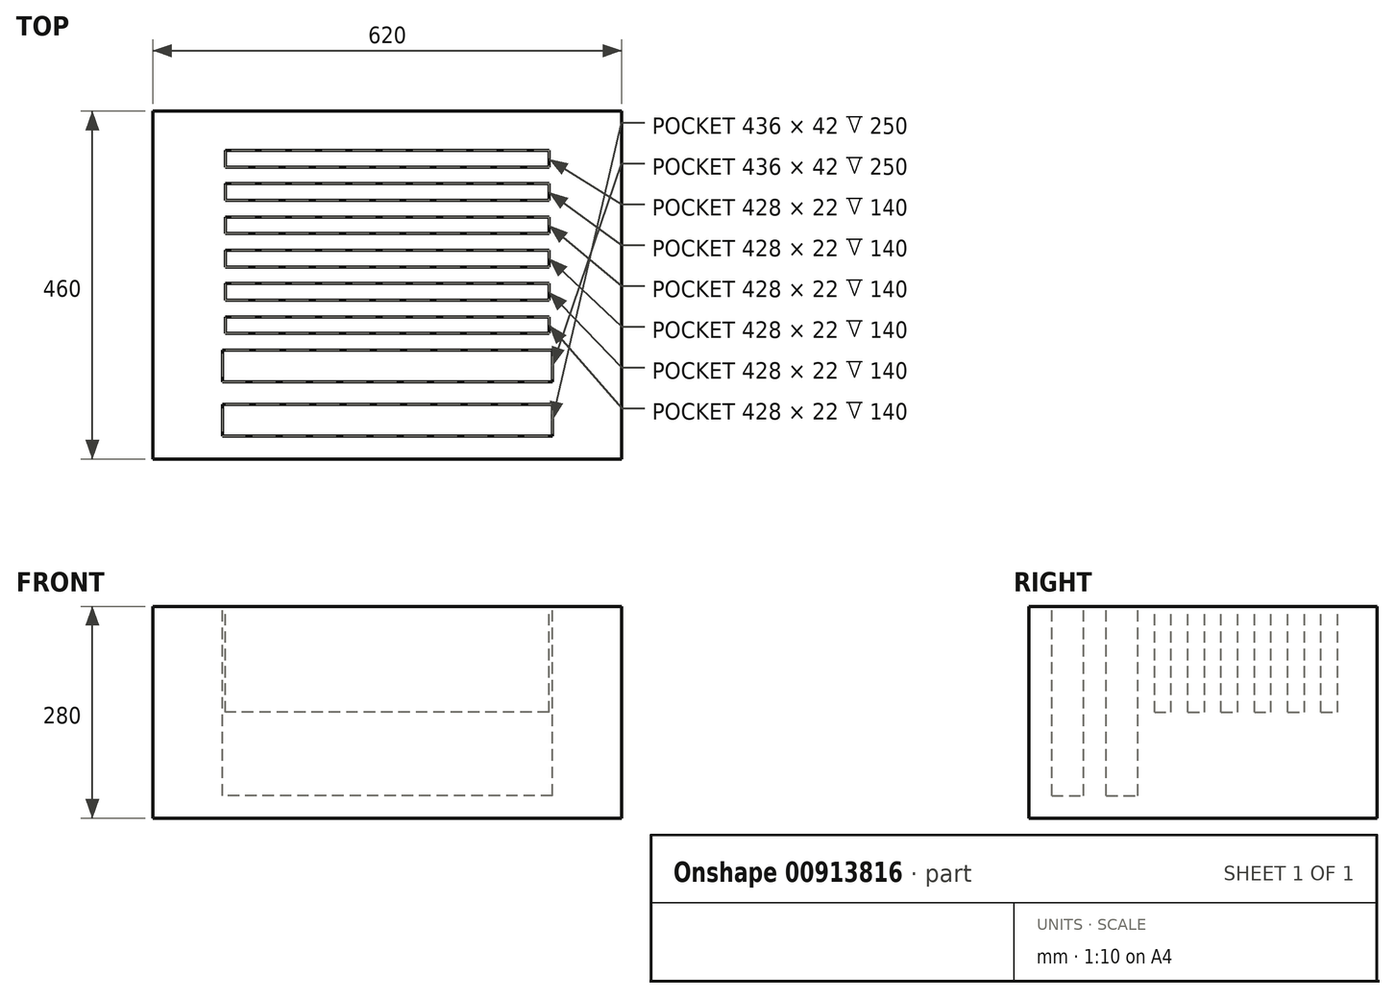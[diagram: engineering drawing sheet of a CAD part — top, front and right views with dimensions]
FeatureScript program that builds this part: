
annotation { "Feature Type Name" : "Feature", "Feature Type Description" : "" }
export const myFeature = defineFeature(function(context is Context, id is Id, definition is map)
    precondition{}
    {
        {
            var Q0;
            Q0=qCreatedBy(makeId("Top.planeOp"),FACE);
            var sketch = newSketch(context, id + "F0", { "sketchPlane" : qUnion([Q0])});
            skLineSegment(sketch, "E0.bottom", {"start": v(310.34, -166) * mm, "end": v(-309.66, -166) * mm});
            skLineSegment(sketch, "E0.top", {"start": v(310.34, 294) * mm, "end": v(-309.66, 294) * mm});
            skLineSegment(sketch, "E0.left", {"start": v(310.34, -166) * mm, "end": v(310.34, 294) * mm});
            skLineSegment(sketch, "E0.right", {"start": v(-309.66, -166) * mm, "end": v(-309.66, 294) * mm});
            skLineSegment(sketch, "E1.bottom", {"start": v(218.34, -136) * mm, "end": v(-217.66, -136) * mm});
            skLineSegment(sketch, "E1.top", {"start": v(218.34, -94) * mm, "end": v(-217.66, -94) * mm});
            skLineSegment(sketch, "E1.left", {"start": v(218.34, -136) * mm, "end": v(218.34, -94) * mm});
            skLineSegment(sketch, "E1.right", {"start": v(-217.66, -136) * mm, "end": v(-217.66, -94) * mm});
            skPoint(sketch, "E1.middle", {"position": v(0, 0) * mm});
            skLineSegment(sketch, "E2.0.1.0", {"start": v(218.34, -64) * mm, "end": v(218.34, -22) * mm});
            skLineSegment(sketch, "E2.0.1.1", {"start": v(218.34, -64) * mm, "end": v(-217.66, -64) * mm});
            skLineSegment(sketch, "E2.0.1.2", {"start": v(218.34, -22) * mm, "end": v(-217.66, -22) * mm});
            skLineSegment(sketch, "E2.0.1.3", {"start": v(-217.66, -64) * mm, "end": v(-217.66, -22) * mm});
            skLineSegment(sketch, "E2.direction1", {"start": v(-217.66, -136) * mm, "end": v(-182.5, -136) * mm, "construction": true});
            skLineSegment(sketch, "E2.direction2", {"start": v(-217.66, -136) * mm, "end": v(-217.66, -64) * mm, "construction": true});
            skLineSegment(sketch, "E3.bottom", {"start": v(214, 0) * mm, "end": v(-214, 0) * mm});
            skLineSegment(sketch, "E3.top", {"start": v(214, 22) * mm, "end": v(-214, 22) * mm});
            skLineSegment(sketch, "E3.left", {"start": v(214, 0) * mm, "end": v(214, 22) * mm});
            skLineSegment(sketch, "E3.right", {"start": v(-214, 0) * mm, "end": v(-214, 22) * mm});
            skPoint(sketch, "E3.middle", {"position": v(0, 11) * mm});
            skLineSegment(sketch, "E4.0.1.0", {"start": v(-214, 44) * mm, "end": v(-214, 66) * mm});
            skLineSegment(sketch, "E4.0.1.1", {"start": v(214, 44) * mm, "end": v(-214, 44) * mm});
            skLineSegment(sketch, "E4.0.1.2", {"start": v(214, 66) * mm, "end": v(-214, 66) * mm});
            skLineSegment(sketch, "E4.0.1.3", {"start": v(214, 44) * mm, "end": v(214, 66) * mm});
            skLineSegment(sketch, "E4.0.2.0", {"start": v(-214, 88) * mm, "end": v(-214, 110) * mm});
            skLineSegment(sketch, "E4.0.2.1", {"start": v(214, 88) * mm, "end": v(-214, 88) * mm});
            skLineSegment(sketch, "E4.0.2.2", {"start": v(214, 110) * mm, "end": v(-214, 110) * mm});
            skLineSegment(sketch, "E4.0.2.3", {"start": v(214, 88) * mm, "end": v(214, 110) * mm});
            skLineSegment(sketch, "E4.0.3.0", {"start": v(-214, 132) * mm, "end": v(-214, 154) * mm});
            skLineSegment(sketch, "E4.0.3.1", {"start": v(214, 132) * mm, "end": v(-214, 132) * mm});
            skLineSegment(sketch, "E4.0.3.2", {"start": v(214, 154) * mm, "end": v(-214, 154) * mm});
            skLineSegment(sketch, "E4.0.3.3", {"start": v(214, 132) * mm, "end": v(214, 154) * mm});
            skLineSegment(sketch, "E4.0.4.0", {"start": v(-214, 176) * mm, "end": v(-214, 198) * mm});
            skLineSegment(sketch, "E4.0.4.1", {"start": v(214, 176) * mm, "end": v(-214, 176) * mm});
            skLineSegment(sketch, "E4.0.4.2", {"start": v(214, 198) * mm, "end": v(-214, 198) * mm});
            skLineSegment(sketch, "E4.0.4.3", {"start": v(214, 176) * mm, "end": v(214, 198) * mm});
            skLineSegment(sketch, "E4.0.5.0", {"start": v(-214, 220) * mm, "end": v(-214, 242) * mm});
            skLineSegment(sketch, "E4.0.5.1", {"start": v(214, 220) * mm, "end": v(-214, 220) * mm});
            skLineSegment(sketch, "E4.0.5.2", {"start": v(214, 242) * mm, "end": v(-214, 242) * mm});
            skLineSegment(sketch, "E4.0.5.3", {"start": v(214, 220) * mm, "end": v(214, 242) * mm});
            skLineSegment(sketch, "E4.direction1", {"start": v(-214, 0) * mm, "end": v(-189, 0) * mm, "construction": true});
            skLineSegment(sketch, "E4.direction2", {"start": v(-214, 0) * mm, "end": v(-214, 44) * mm, "construction": true});
            skSolve(sketch);
        }
        {
            var Q0;
            Q0=makeQuery(id+"F0.imprint","IMPRINT",FACE,{"disambiguationData":[TD([[makeQuery(id+"F0.imprint","IMPRINT",EDGE,{"derivedFrom":sQuery(id+"F0.wireOp",EDGE,"E0.bottom")}),-1.0]])]});
            var Q1;
            Q1=makeQuery(id+"F0.imprint","IMPRINT",FACE,{"disambiguationData":[TD([[makeQuery(id+"F0.imprint","IMPRINT",EDGE,{"derivedFrom":sQuery(id+"F0.wireOp",EDGE,"E2.0.2.0")}),1.0]])]});
            var Q2;
            Q2=makeQuery(id+"F0.imprint","IMPRINT",FACE,{"disambiguationData":[TD([[makeQuery(id+"F0.imprint","IMPRINT",EDGE,{"derivedFrom":sQuery(id+"F0.wireOp",EDGE,"E2.0.1.0")}),1.0]])]});
            var Q3;
            Q3=makeQuery(id+"F0.imprint","IMPRINT",FACE,{"disambiguationData":[TD([[makeQuery(id+"F0.imprint","IMPRINT",EDGE,{"derivedFrom":sQuery(id+"F0.wireOp",EDGE,"E1.bottom")}),-1.0]])]});
            var Q4;
            Q4=makeQuery(id+"F0.imprint","IMPRINT",FACE,{"disambiguationData":[TD([[makeQuery(id+"F0.imprint","IMPRINT",EDGE,{"derivedFrom":sQuery(id+"F0.wireOp",EDGE,"E3.bottom")}),-1.0]])]});
            var Q5;
            Q5=makeQuery(id+"F0.imprint","IMPRINT",FACE,{"disambiguationData":[TD([[makeQuery(id+"F0.imprint","IMPRINT",EDGE,{"derivedFrom":sQuery(id+"F0.wireOp",EDGE,"E4.0.1.0")}),-1.0]])]});
            var Q6;
            Q6=makeQuery(id+"F0.imprint","IMPRINT",FACE,{"disambiguationData":[TD([[makeQuery(id+"F0.imprint","IMPRINT",EDGE,{"derivedFrom":sQuery(id+"F0.wireOp",EDGE,"E4.0.2.0")}),-1.0]])]});
            var Q7;
            Q7=makeQuery(id+"F0.imprint","IMPRINT",FACE,{"disambiguationData":[TD([[makeQuery(id+"F0.imprint","IMPRINT",EDGE,{"derivedFrom":sQuery(id+"F0.wireOp",EDGE,"E4.0.3.0")}),-1.0]])]});
            var Q8;
            Q8=makeQuery(id+"F0.imprint","IMPRINT",FACE,{"disambiguationData":[TD([[makeQuery(id+"F0.imprint","IMPRINT",EDGE,{"derivedFrom":sQuery(id+"F0.wireOp",EDGE,"E4.0.4.0")}),-1.0]])]});
            var Q9;
            Q9=makeQuery(id+"F0.imprint","IMPRINT",FACE,{"disambiguationData":[TD([[makeQuery(id+"F0.imprint","IMPRINT",EDGE,{"derivedFrom":sQuery(id+"F0.wireOp",EDGE,"E4.0.5.0")}),-1.0]])]});
            extrude(context, id + "F1", {"entities" : qUnion([Q0, Q1, Q2, Q3, Q4, Q5, Q6, Q7, Q8, Q9]), "oppositeDirection" : true, "depth" : 280 * mm, "offsetDistance" : 25 * mm});
        }
        {
            var Q0;
            Q0=makeQuery(id+"F0.imprint","IMPRINT",FACE,{"disambiguationData":[TD([[makeQuery(id+"F0.imprint","IMPRINT",EDGE,{"derivedFrom":sQuery(id+"F0.wireOp",EDGE,"E2.0.1.0")}),1.0]])]});
            var Q1;
            Q1=makeQuery(id+"F0.imprint","IMPRINT",FACE,{"disambiguationData":[TD([[makeQuery(id+"F0.imprint","IMPRINT",EDGE,{"derivedFrom":sQuery(id+"F0.wireOp",EDGE,"E1.bottom")}),-1.0]])]});
            extrude(context, id + "F2", {"entities" : qUnion([Q0, Q1]), "operationType" : NewBodyOperationType.REMOVE, "oppositeDirection" : true, "depth" : 250 * mm, "offsetDistance" : 25 * mm});
        }
        {
            var Q0;
            Q0=makeQuery(id+"F0.imprint","IMPRINT",FACE,{"disambiguationData":[TD([[makeQuery(id+"F0.imprint","IMPRINT",EDGE,{"derivedFrom":sQuery(id+"F0.wireOp",EDGE,"E3.bottom")}),-1.0]])]});
            var Q1;
            Q1=makeQuery(id+"F0.imprint","IMPRINT",FACE,{"disambiguationData":[TD([[makeQuery(id+"F0.imprint","IMPRINT",EDGE,{"derivedFrom":sQuery(id+"F0.wireOp",EDGE,"E4.0.1.0")}),-1.0]])]});
            var Q2;
            Q2=makeQuery(id+"F0.imprint","IMPRINT",FACE,{"disambiguationData":[TD([[makeQuery(id+"F0.imprint","IMPRINT",EDGE,{"derivedFrom":sQuery(id+"F0.wireOp",EDGE,"E4.0.2.0")}),-1.0]])]});
            var Q3;
            Q3=makeQuery(id+"F0.imprint","IMPRINT",FACE,{"disambiguationData":[TD([[makeQuery(id+"F0.imprint","IMPRINT",EDGE,{"derivedFrom":sQuery(id+"F0.wireOp",EDGE,"E4.0.3.0")}),-1.0]])]});
            var Q4;
            Q4=makeQuery(id+"F0.imprint","IMPRINT",FACE,{"disambiguationData":[TD([[makeQuery(id+"F0.imprint","IMPRINT",EDGE,{"derivedFrom":sQuery(id+"F0.wireOp",EDGE,"E4.0.4.0")}),-1.0]])]});
            var Q5;
            Q5=makeQuery(id+"F0.imprint","IMPRINT",FACE,{"disambiguationData":[TD([[makeQuery(id+"F0.imprint","IMPRINT",EDGE,{"derivedFrom":sQuery(id+"F0.wireOp",EDGE,"E4.0.5.0")}),-1.0]])]});
            extrude(context, id + "F3", {"entities" : qUnion([Q0, Q1, Q2, Q3, Q4, Q5]), "operationType" : NewBodyOperationType.REMOVE, "oppositeDirection" : true, "depth" : 140 * mm, "offsetDistance" : 25 * mm});
        }
    });
